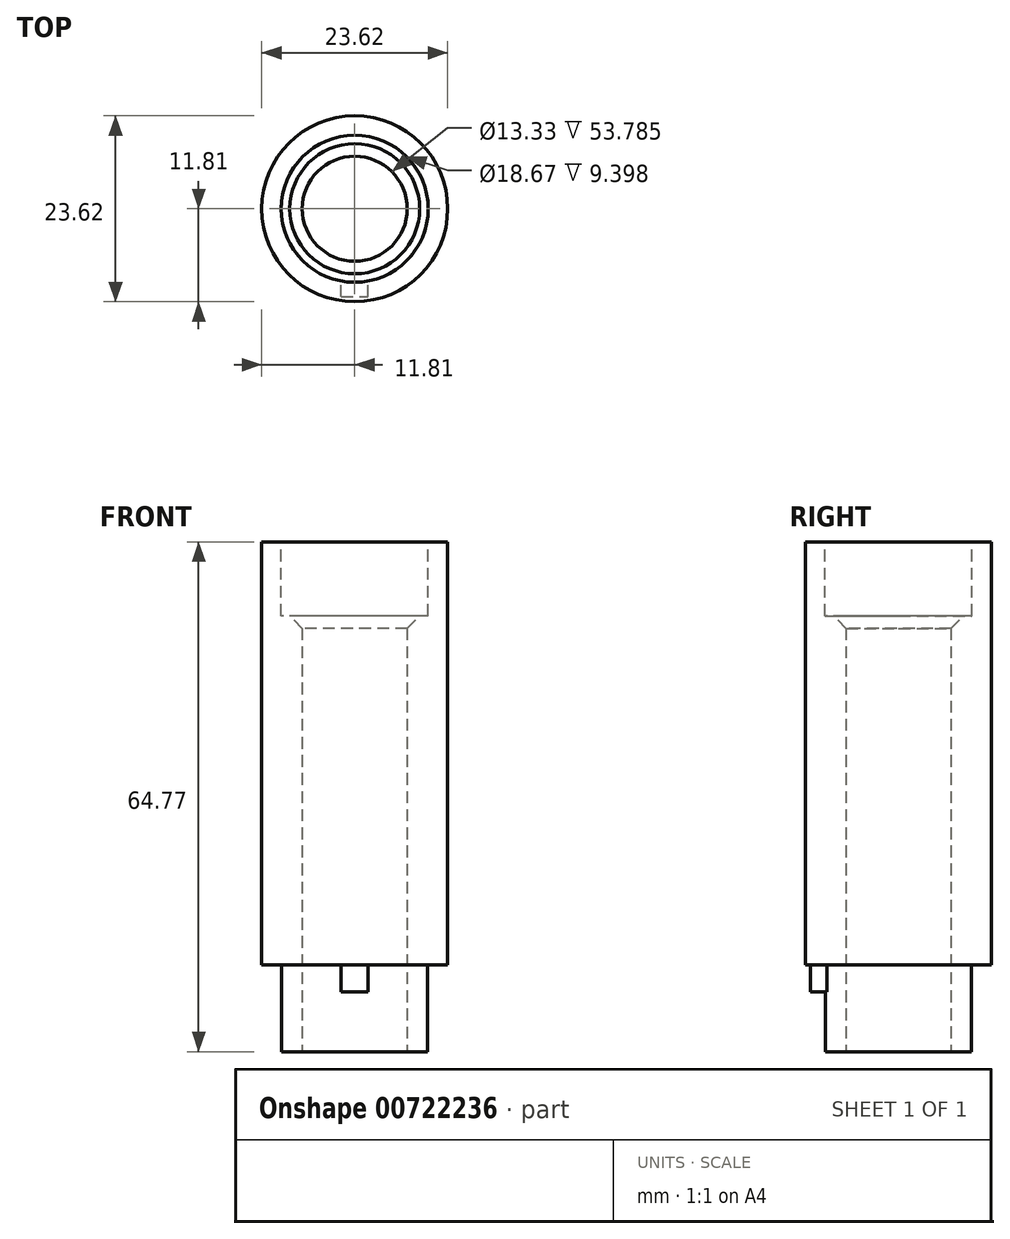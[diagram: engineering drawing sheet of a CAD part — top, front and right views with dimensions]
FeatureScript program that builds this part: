
annotation { "Feature Type Name" : "Feature", "Feature Type Description" : "" }
export const myFeature = defineFeature(function(context is Context, id is Id, definition is map)
    precondition{}
    {
        {
            var Q0;
            Q0=qCreatedBy(makeId("Top.planeOp"),FACE);
            var sketch = newSketch(context, id + "F0", { "sketchPlane" : qUnion([Q0])});
            skCircle(sketch, "E0", {"center": v(0, 0) * mm, "radius": 11.81 * mm});
            skCircle(sketch, "E1", {"center": v(0, 0) * mm, "radius": 6.67 * mm});
            skSolve(sketch);
        }
        {
            var Q0;
            Q0 = qSketchRegion(id + "F0", true);
            extrude(context, id + "F1", {"entities" : qUnion([Q0]), "depth" : 64.77 * mm, "offsetDistance" : 25.4 * mm});
        }
        {
            var Q0;
            Q0=makeQuery(id+"F1.opExtrude","CAP_FACE",FACE,{"disambiguationData":[OSD([sQuery(id+"F0.wireOp",EDGE,"E0"),sQuery(id+"F0.wireOp",EDGE,"E1")])],"isStart":true});
            var sketch = newSketch(context, id + "F2", { "sketchPlane" : qUnion([Q0])});
            skCircle(sketch, "E2", {"center": v(0, 0) * mm, "radius": 9.27 * mm});
            skSolve(sketch);
        }
        {
            var Q0;
            Q0=makeQuery(id+"F2.imprint","IMPRINT",FACE,{"disambiguationData":[TD([[makeQuery(id+"F2.imprint","IMPRINT",EDGE,{"derivedFrom":makeQuery(id+"F1.opExtrude","CAP_EDGE",EDGE,{"disambiguationData":[OSD([sQuery(id+"F0.wireOp",EDGE,"E1")])],"isStart":true})}),-1.0]])]});
            var Q1;
            Q1=makeQuery(id+"F2.imprint","IMPRINT",FACE,{"disambiguationData":[TD([[makeQuery(id+"F2.imprint","IMPRINT",EDGE,{"derivedFrom":sQuery(id+"F2.wireOp",EDGE,"E2")}),-1.0]])]});
            extrude(context, id + "F3", {"entities" : qUnion([Q0, Q1]), "operationType" : NewBodyOperationType.REMOVE, "oppositeDirection" : true, "depth" : 11.05 * mm, "offsetDistance" : 25.4 * mm});
        }
        {
            var Q0;
            Q0=makeQuery(id+"F3.boolean.opBoolean","COPY",FACE,{"derivedFrom":makeQuery(id+"F3.opExtrude","CAP_FACE",FACE,{"disambiguationData":[OSD([sQuery(id+"F0.wireOp",EDGE,"E0"),sQuery(id+"F2.wireOp",EDGE,"E2")])],"isStart":false})});
            var sketch = newSketch(context, id + "F4", { "sketchPlane" : qUnion([Q0])});
            skLineSegment(sketch, "E3.bottom", {"start": v(-1.71, 11.18) * mm, "end": v(1.71, 11.18) * mm});
            skLineSegment(sketch, "E3.left", {"start": v(-1.71, 11.18) * mm, "end": v(-1.71, 9.11) * mm});
            skLineSegment(sketch, "E3.right", {"start": v(1.71, 11.18) * mm, "end": v(1.71, 9.11) * mm});
            skLineSegment(sketch, "E4", {"start": v(0, 0) * mm, "end": v(0, 11.18) * mm, "construction": true});
            skArc(sketch, "E5", {"start": v(1.71, 9.11) * mm, "mid": v(0, 9.27) * mm, "end": v(-1.71, 9.11) * mm});
            skSolve(sketch);
        }
        {
            var Q0;
            Q0 = qSketchRegion(id + "F4", true);
            extrude(context, id + "F5", {"entities" : qUnion([Q0]), "operationType" : NewBodyOperationType.ADD, "depth" : 3.43 * mm, "offsetDistance" : 25.4 * mm});
        }
        {
            var Q0;
            Q0=makeQuery(id+"F1.opExtrude","CAP_FACE",FACE,{"disambiguationData":[OSD([sQuery(id+"F0.wireOp",EDGE,"E0"),sQuery(id+"F0.wireOp",EDGE,"E1")])],"isStart":false});
            var sketch = newSketch(context, id + "F6", { "sketchPlane" : qUnion([Q0])});
            skCircle(sketch, "E6", {"center": v(0, 0) * mm, "radius": 9.33 * mm});
            skSolve(sketch);
        }
        {
            var Q0;
            Q0 = qSketchRegion(id + "F6", true);
            extrude(context, id + "F7", {"entities" : qUnion([Q0]), "operationType" : NewBodyOperationType.REMOVE, "oppositeDirection" : true, "depth" : 9.4 * mm, "offsetDistance" : 25.4 * mm});
        }
        {
            var Q0;
            Q0=makeQuery(id+"F7.boolean.opBoolean","INTERSECT",EDGE,{"derivedFrom":[makeQuery(id+"F1.opExtrude","SWEPT_FACE",FACE,{"disambiguationData":[OSD([sQuery(id+"F0.wireOp",EDGE,"E1")])]}),makeQuery(id+"F7.opExtrude","CAP_FACE",FACE,{"disambiguationData":[OSD([sQuery(id+"F6.wireOp",EDGE,"E6")])],"isStart":false})]});
            chamfer(context, id + "F8", {"entities" : qUnion([Q0]), "width" : 1.59 * mm, "tangentPropagation" : true});
        }
    });
